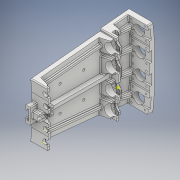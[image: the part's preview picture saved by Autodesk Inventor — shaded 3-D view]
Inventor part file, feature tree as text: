
AUTODESK INVENTOR PART (.ipt)
format: ipt  version: 2019 (Build 230136000, 136)  size: 2,217,472 bytes
history: native  units: mm
features: extrude x26, sketch x13, other x9, projected_geometry x7, fillet x6, draft x5, hole x2, split x2, thicken_offset x2, reference x2, revolve x1, pattern_linear x1, move_body x1, plane x1, boolean_combine x1, loft x1, mirror x1
ambient origin geometry x8: Origin, YZ Plane, XZ Plane, XY Plane, X Axis, Y Axis, Z Axis, Center Point
bodies: Solid5 (feature_tree)
feature tree (81):
  other  "holder1"
  sketch  "Sketch3"  dims[d0=26.07mm d1=32.0mm]
  extrude  "Extrusion2"  Depth=32.0mm
  extrude  "Extrusion4"  Depth=162.501mm
  extrude  "Extrusion5"  Depth=10.645mm
  revolve  "Revolution1"  [1 undecoded]
  fillet  "Fillet1"  Radius=162.501mm
  extrude  "Extrusion7"  Depth=6.499mm
  extrude  "Extrusion8"  Depth=2.0mm TaperAngle=0.0deg
  fillet  "Fillet2"  Radius=2.0mm
  sketch  "Sketch15"  dims[d7=0.0mm d11=10.645mm]
  extrude  "Extrusion19"  Depth=5.0mm
  extrude  "Extrusion20"  Depth=24.0mm
  extrude  "Extrusion21"  Depth=8.0mm TaperAngle=0.0deg
  other  "draft"
  sketch  "Sketch16"  dims[d12=169.0mm d13=10.7mm d14=162.501mm]
  extrude  "Extrusion40"  Depth=2.0mm
  extrude  "Extrusion30"  Depth=0.5mm
  extrude  "Extrusion28"  Depth=10.0mm TaperAngle=0.0deg
  extrude  "Extrusion22"  Depth=2.0mm
  hole  "Hole3"  [1 undecoded]
  draft  "FaceDraft3"
  draft  "FaceDraft4"
  draft  "FaceDraft5"
  pattern_linear  "Rectangular Pattern4"  Spacing1=45.0mm  [1 undecoded]
  move_body  "Move Body3"
  plane  "Work Plane3"
  split  "Split1"
  split  "Split2"
  boolean_combine  "Combine2"
  loft  "Loft2"
  extrude  "Extrusion41"  Depth=2.0mm TaperAngle=0.0deg
  extrude  "Extrusion32"  Depth=2.0mm
  mirror  "Mirror3"
  sketch  "Sketch30"  dims[d18=90.0deg d19=6.0mm d20=0.0mm d21=2.0mm]
  extrude  "Extrusion34"  Depth=2.0mm
  extrude  "Extrusion35"  Depth=2.0mm
  draft  "FaceDraft6"
  draft  "FaceDraft7"
  hole  "Hole6"  [1 undecoded]
  extrude  "Extrusion36"  TaperAngle=15.0deg  [1 undecoded]
  sketch  "Sketch32"  dims[d24=30.656mm d25=24.0mm]
  extrude  "Extrusion44"  TaperAngle=15.0deg  [1 undecoded]
  extrude  "Extrusion45"  Depth=2.0mm
  fillet  "Fillet17"  Radius=5.0mm
  extrude  "Extrusion48"  Depth=2.0mm TaperAngle=0.0deg
  extrude  "Extrusion49"  Depth=2.0mm
  fillet  "Fillet18"  Radius=20.0mm
  sketch  "Sketch41"  dims[d31=7.0mm d32=0.0mm d33=1.0mm d34=2.0mm]
  extrude  "Extrusion51"  Depth=2.0mm
  extrude  "Extrusion52"  Depth=2.0mm
  sketch  "Sketch43"  dims[d43=28.0mm d44=0.5mm]
  extrude  "Extrusion53"  Depth=2.0mm
  extrude  "Extrusion54"  Depth=2.0mm TaperAngle=0.0deg
  fillet  "Fillet20"  Radius=60.0mm
  extrude  "Extrusion55"  Depth=2.0mm
  thicken_offset  "Thicken8"
  thicken_offset  "Thicken9"
  fillet  "Fillet22"  Radius=8.0mm
  sketch  "Sketch45"  dims[d136=57.75mm d137=0.0mm d138=40.0mm d139=6.5mm d140=45.0mm d141=0.0mm d142=23.0mm d143=74.5mm d144=0.0mm d145=31.0mm d146=3.4mm d147=6.0mm d148=4.0mm d149=2.0mm d150=90.0deg d151=18.75mm d152=0.0mm d153=42.0mm d154=28.0mm d155=9.5mm d182=15.0deg d183=15.0deg d199=5.0mm d201=5.0mm d202=8.0mm d203=0.0mm d224=8.0mm d227=20.0mm d228=0.0mm d229=5.0mm d230=20.0mm d232=20.0mm d234=42.0mm d238=2.0mm d239=0.0mm d242=60.0mm d243=55.0mm d244=8.0mm d245=6.0mm d246=0.0mm d247=10.9mm d248=0.0mm d249=5.5mm d250=6.0mm d251=4.0mm d252=2.0mm d253=90.0deg d254=8.0mm d255=20.594885mm d261=8.0mm d262=6.0mm d263=17.0mm d264=0.0mm d265=8.0mm d268=6.0mm d271=6.0mm d274=10.0mm d284=4.0mm d285=0.0mm d286=0.959931mm d291=0.0mm d292=90.0deg d293=0.0mm d294=90.0deg d295=10.0mm d296=0.0mm d299=14.9mm d302=16.9mm d303=10.0mm d304=0.0mm d305=10.0mm d306=0.0mm d308=8.2mm d315=16.0mm d316=13.035mm d317=25.346mm d318=0.0mm d319=1.5mm d320=1.9mm d324=2.0mm d325=0.0mm d326=2.0mm d327=0.0mm d330=1.0mm d331=20.0mm d332=50.0mm d333=13.0mm d334=8.0mm d335=16.0mm d336=0.0mm d337=8.0mm d338=0.0mm d343=4.0mm d344=8.0mm d345=0.0mm d346=1.0mm d348=4.0mm d349=15.0mm d350=0.0mm d353=10.1mm d354=37.0mm d355=7.0mm d356=20.0mm d357=2.1mm d358=0.0mm d359=2.0mm d360=2.0mm d361=2.0mm d362=2.0mm d363=55.0mm d364=18.0mm d365=1.745329mm d367=2.0mm d368=2.0mm d371=42.0mm d372=8.0mm d373=2.0mm d374=0.5mm d375=2.0mm d376=15.0deg d377=15.0deg d378=2.0mm d209=1.0mm d210=1.0mm d222=1.0mm d223=1.0mm]
  sketch  "Sketch5"  dims[d5=150.644mm d6=162.501mm]
  projected_geometry  "Projected Loop3"
  sketch  "Sketch29"  dims[d15=5.0mm d16=0.0mm d17=6.499mm]
  projected_geometry  "Projected Loop9"
  projected_geometry  "Projected Loop10"
  sketch  "Sketch31"  dims[d22=42.0mm d23=5.0mm]
  projected_geometry  "Projected Loop11"
  other  "Pattern of holder1:3"
  other  "Edges3"
  other  "Edges4"
  sketch  "Sketch40"  dims[d26=25.0mm d29=8.0mm d30=0.0mm]
  projected_geometry  "Projected Loop17"
  projected_geometry  "Projected Loop18"
  sketch  "Sketch44"  dims[d78=22.0mm d134=10.0mm d135=0.0mm]
  projected_geometry  "Projected Loop19"
  reference  "Reference1"
  reference  "Reference2"
  parser-record x1  (decoder bookkeeping rows leaked as tree rows — omitted from the tree; the rows remain in map.json)
  other  "zplate_assembly.iam"
  other  "NORDSONEFD-7012001 BARREL O 55CC CL:3"
  other  "NORDSONEFD-7012001 BARREL O 55CC CL:4"
note: 6 required parameter values undecoded (feature->parameter linkage not recoverable at this tier; creation-order binding heuristic only, values carry confidence <= 0.55)
note: 1 file-system path scrubbed to <path> (originals preserved in map.json)